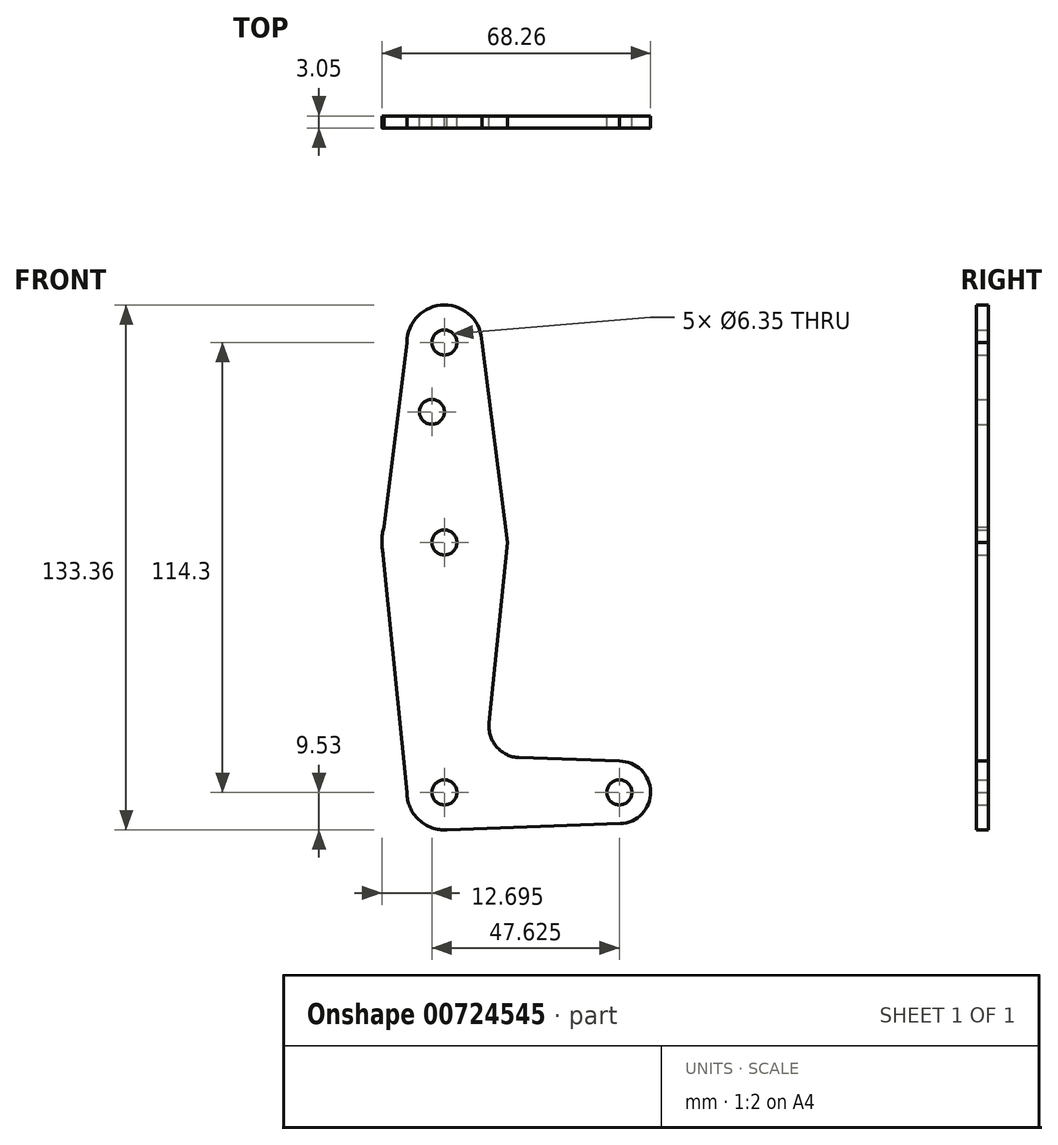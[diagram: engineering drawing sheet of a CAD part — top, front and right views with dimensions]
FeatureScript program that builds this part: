
annotation { "Feature Type Name" : "Feature", "Feature Type Description" : "" }
export const myFeature = defineFeature(function(context is Context, id is Id, definition is map)
    precondition{}
    {
        {
            var Q0;
            Q0=qCreatedBy(makeId("Front.planeOp"),FACE);
            var sketch = newSketch(context, id + "F0", { "sketchPlane" : qUnion([Q0])});
            skLineSegment(sketch, "E0", {"start": v(0, 0) * mm, "end": v(0, 63.5) * mm, "construction": true});
            skLineSegment(sketch, "E1", {"start": v(0, 0) * mm, "end": v(44.45, 0) * mm, "construction": true});
            skCircle(sketch, "E2", {"center": v(0, 63.5) * mm, "radius": 15.88 * mm});
            skLineSegment(sketch, "E3", {"start": v(0, 63.5) * mm, "end": v(0, 114.3) * mm, "construction": true});
            skCircle(sketch, "E4", {"center": v(0, 114.3) * mm, "radius": 9.52 * mm});
            skCircle(sketch, "E5", {"center": v(44.45, 0) * mm, "radius": 7.94 * mm});
            skCircle(sketch, "E6", {"center": v(0, 0) * mm, "radius": 9.52 * mm});
            skLineSegment(sketch, "E7", {"start": v(-9.52, 114.3) * mm, "end": v(-15.87, 63.5) * mm});
            skLineSegment(sketch, "E8", {"start": v(9.53, 114.3) * mm, "end": v(16, 63.5) * mm});
            skLineSegment(sketch, "E9", {"start": v(-15.87, 63.5) * mm, "end": v(-9.52, 0) * mm});
            skLineSegment(sketch, "E10", {"start": v(16, 63.5) * mm, "end": v(11.36, 17.6) * mm});
            skLineSegment(sketch, "E11", {"start": v(18.98, 8.85) * mm, "end": v(44.45, 7.94) * mm});
            skLineSegment(sketch, "E12", {"start": v(0, -9.52) * mm, "end": v(44.73, -7.93) * mm});
            skCircle(sketch, "E13", {"center": v(0, 114.3) * mm, "radius": 3.18 * mm});
            skCircle(sketch, "E14", {"center": v(0, 63.5) * mm, "radius": 3.18 * mm});
            skCircle(sketch, "E15", {"center": v(0, 0) * mm, "radius": 3.18 * mm});
            skCircle(sketch, "E16", {"center": v(44.45, 0) * mm, "radius": 3.18 * mm});
            skCircle(sketch, "E17", {"center": v(-3.18, 96.7) * mm, "radius": 3.18 * mm});
            skPoint(sketch, "E18.newPointA", {"position": v(9.57, 0) * mm});
            skPoint(sketch, "E18.newPointB", {"position": v(0, 9.53) * mm});
            skArc(sketch, "E18.filletArc", {"start": v(11.36, 17.6) * mm, "mid": v(13.27, 11.57) * mm, "end": v(18.98, 8.85) * mm});
            skSolve(sketch);
        }
        {
            var Q0;
            Q0 = qSketchRegion(id + "F0", true);
            extrude(context, id + "F1", {"entities" : qUnion([Q0]), "depth" : 3.05 * mm, "offsetDistance" : 25.4 * mm});
        }
    });
